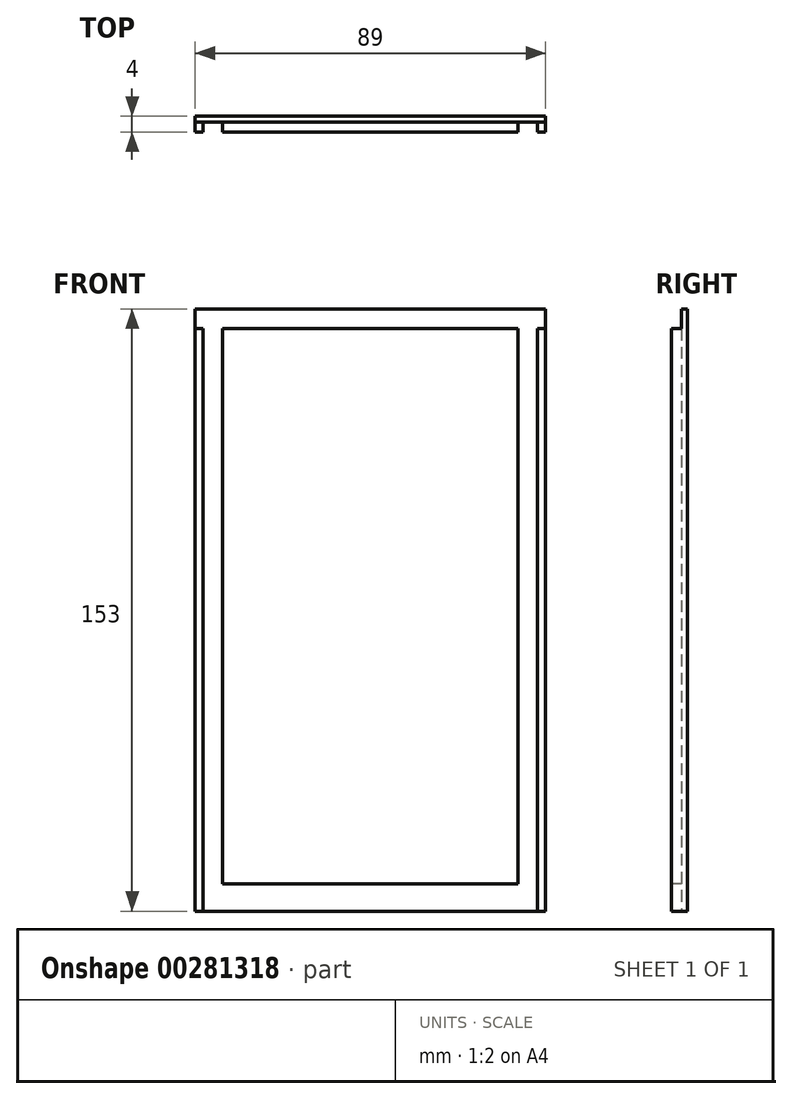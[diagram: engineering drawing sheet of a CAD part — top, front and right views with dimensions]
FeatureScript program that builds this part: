
annotation { "Feature Type Name" : "Feature", "Feature Type Description" : "" }
export const myFeature = defineFeature(function(context is Context, id is Id, definition is map)
    precondition{}
    {
        {
            var Q0;
            Q0=qCreatedBy(makeId("Front.planeOp"),FACE);
            var sketch = newSketch(context, id + "F0", { "sketchPlane" : qUnion([Q0])});
            skLineSegment(sketch, "E0.bottom", {"start": v(44.5, -76.5) * mm, "end": v(-44.5, -76.5) * mm});
            skLineSegment(sketch, "E0.top", {"start": v(44.5, 76.5) * mm, "end": v(-44.5, 76.5) * mm});
            skLineSegment(sketch, "E0.left", {"start": v(44.5, -76.5) * mm, "end": v(44.5, 76.5) * mm});
            skLineSegment(sketch, "E0.right", {"start": v(-44.5, -76.5) * mm, "end": v(-44.5, 76.5) * mm});
            skPoint(sketch, "E0.middle", {"position": v(0, 0) * mm});
            skSolve(sketch);
        }
        {
            var Q0;
            Q0 = qSketchRegion(id + "F0", true);
            extrude(context, id + "F1", {"entities" : qUnion([Q0]), "depth" : 4 * mm});
        }
        {
            var Q0;
            Q0=makeQuery(id+"F1.opExtrude","CAP_FACE",FACE,{"disambiguationData":[OSD([sQuery(id+"F0.wireOp",EDGE,"E0.bottom"),sQuery(id+"F0.wireOp",EDGE,"E0.top"),sQuery(id+"F0.wireOp",EDGE,"E0.left"),sQuery(id+"F0.wireOp",EDGE,"E0.right")])],"isStart":false});
            var sketch = newSketch(context, id + "F2", { "sketchPlane" : qUnion([Q0])});
            skLineSegment(sketch, "E1.bottom", {"start": v(-42.5, 76.5) * mm, "end": v(-37.5, 76.5) * mm});
            skLineSegment(sketch, "E1.top", {"start": v(-42.5, -76.5) * mm, "end": v(-37.5, -76.5) * mm});
            skLineSegment(sketch, "E1.left", {"start": v(-42.5, 76.5) * mm, "end": v(-42.5, -76.5) * mm});
            skLineSegment(sketch, "E1.right", {"start": v(-37.5, 76.5) * mm, "end": v(-37.5, -76.5) * mm});
            skLineSegment(sketch, "E2.bottom", {"start": v(42.5, 76.5) * mm, "end": v(37.5, 76.5) * mm});
            skLineSegment(sketch, "E2.top", {"start": v(42.5, -76.5) * mm, "end": v(37.5, -76.5) * mm});
            skLineSegment(sketch, "E2.left", {"start": v(42.5, 76.5) * mm, "end": v(42.5, -76.5) * mm});
            skLineSegment(sketch, "E2.right", {"start": v(37.5, 76.5) * mm, "end": v(37.5, -76.5) * mm});
            skLineSegment(sketch, "E3.bottom", {"start": v(-37.5, -76.5) * mm, "end": v(37.5, -76.5) * mm});
            skLineSegment(sketch, "E3.top", {"start": v(-37.5, -69.5) * mm, "end": v(37.5, -69.5) * mm});
            skLineSegment(sketch, "E3.left", {"start": v(-37.5, -76.5) * mm, "end": v(-37.5, -69.5) * mm});
            skLineSegment(sketch, "E3.right", {"start": v(37.5, -76.5) * mm, "end": v(37.5, -69.5) * mm});
            skLineSegment(sketch, "E4.left", {"start": v(-37.5, 76.5) * mm, "end": v(-37.5, 71.5) * mm});
            skLineSegment(sketch, "E5.bottom", {"start": v(-44.5, 76.5) * mm, "end": v(44.5, 76.5) * mm});
            skLineSegment(sketch, "E5.top", {"start": v(-44.5, 71.5) * mm, "end": v(44.5, 71.5) * mm});
            skLineSegment(sketch, "E5.left", {"start": v(-44.5, 76.5) * mm, "end": v(-44.5, 71.5) * mm});
            skLineSegment(sketch, "E5.right", {"start": v(44.5, 76.5) * mm, "end": v(44.5, 71.5) * mm});
            skSolve(sketch);
        }
        {
            var Q0;
            Q0 = qSketchRegion(id + "F2", true);
            extrude(context, id + "F3", {"entities" : qUnion([Q0]), "operationType" : NewBodyOperationType.REMOVE, "oppositeDirection" : true, "depth" : 2.5 * mm});
        }
    });
